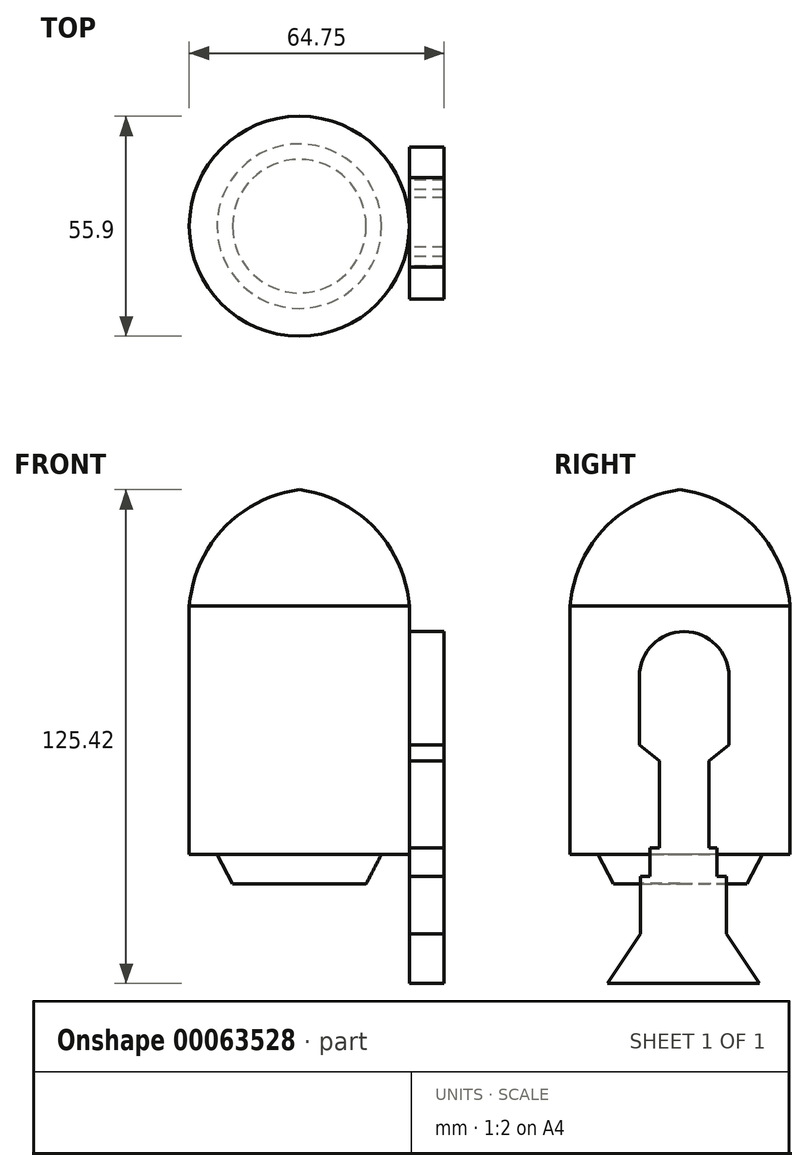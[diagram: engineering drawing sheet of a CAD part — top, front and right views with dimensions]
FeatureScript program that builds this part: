
annotation { "Feature Type Name" : "Feature", "Feature Type Description" : "" }
export const myFeature = defineFeature(function(context is Context, id is Id, definition is map)
    precondition{}
    {
        {
            var Q0;
            Q0=qCreatedBy(makeId("Front.planeOp"),FACE);
            var sketch = newSketch(context, id + "F0", { "sketchPlane" : qUnion([Q0])});
            skLineSegment(sketch, "E0", {"start": v(0, 29.6) * mm, "end": v(0, -70.4) * mm});
            skArc(sketch, "E1", {"start": v(27.95, 0) * mm, "mid": v(19.23, 19.76) * mm, "end": v(0, 29.6) * mm});
            skLineSegment(sketch, "E2", {"start": v(27.95, 0) * mm, "end": v(27.95, -63.03) * mm});
            skLineSegment(sketch, "E3", {"start": v(27.95, -63.03) * mm, "end": v(20.9, -63.03) * mm});
            skLineSegment(sketch, "E4", {"start": v(20.9, -63.03) * mm, "end": v(16.98, -70.53) * mm});
            skLineSegment(sketch, "E5", {"start": v(16.98, -70.53) * mm, "end": v(0, -70.4) * mm});
            skSolve(sketch);
        }
        {
            var Q0;
            Q0=makeQuery(id+"F0.imprint","IMPRINT",FACE,{"disambiguationData":[TD([[makeQuery(id+"F0.imprint","IMPRINT",EDGE,{"derivedFrom":sQuery(id+"F0.wireOp",EDGE,"E0")}),1.0]])]});
            var Q1;
            Q1=sQuery(id+"F0.wireOp",EDGE,"E0");
            revolve(context, id + "F1", {"entities" : qUnion([Q0]), "axis" : qUnion([Q1]), "revolveType" : RevolveType.FULL});
        }
        {
            var Q0;
            Q0=qCreatedBy(makeId("Right.planeOp"),FACE);
            cPlane(context, id + "F2", {"entities" : qUnion([Q0]), "cplaneType" : CPlaneType.OFFSET, "offset" : 28 * mm, "width" : 150 * mm, "height" : 150 * mm});
        }
        {
            var Q0;
            Q0=qCreatedBy(id+"F2.planeOp",FACE);
            var sketch = newSketch(context, id + "F3", { "sketchPlane" : qUnion([Q0])});
            skLineSegment(sketch, "E6", {"start": v(-10.35, -35.3) * mm, "end": v(-5.27, -39.28) * mm});
            skLineSegment(sketch, "E7", {"start": v(-5.27, -39.28) * mm, "end": v(-5.27, -61.37) * mm});
            skLineSegment(sketch, "E8", {"start": v(-5.27, -61.37) * mm, "end": v(-7.7, -61.37) * mm});
            skLineSegment(sketch, "E9", {"start": v(-7.7, -61.37) * mm, "end": v(-7.7, -68.65) * mm});
            skLineSegment(sketch, "E10", {"start": v(-7.7, -68.65) * mm, "end": v(-10.13, -68.65) * mm});
            skLineSegment(sketch, "E11", {"start": v(-10.13, -68.65) * mm, "end": v(-10.13, -83.23) * mm});
            skLineSegment(sketch, "E12", {"start": v(-10.13, -83.23) * mm, "end": v(-18.52, -95.82) * mm});
            skLineSegment(sketch, "E13", {"start": v(-18.52, -95.82) * mm, "end": v(20.13, -95.82) * mm});
            skLineSegment(sketch, "E14", {"start": v(20.13, -95.82) * mm, "end": v(11.74, -83.23) * mm});
            skLineSegment(sketch, "E15", {"start": v(11.74, -83.23) * mm, "end": v(11.74, -68.65) * mm});
            skLineSegment(sketch, "E16", {"start": v(11.74, -68.65) * mm, "end": v(9.31, -68.65) * mm});
            skLineSegment(sketch, "E17", {"start": v(9.31, -68.65) * mm, "end": v(9.31, -61.37) * mm});
            skLineSegment(sketch, "E18", {"start": v(9.31, -61.37) * mm, "end": v(7.32, -61.37) * mm});
            skLineSegment(sketch, "E19", {"start": v(7.32, -61.37) * mm, "end": v(7.32, -39.28) * mm});
            skLineSegment(sketch, "E20", {"start": v(7.32, -39.28) * mm, "end": v(12.4, -35.3) * mm});
            skLineSegment(sketch, "E21", {"start": v(12.4, -35.3) * mm, "end": v(12.4, -17.86) * mm});
            skLineSegment(sketch, "E22", {"start": v(-10.35, -35.3) * mm, "end": v(-10.35, -17.86) * mm});
            skArc(sketch, "E23", {"start": v(12.4, -17.86) * mm, "mid": v(1.03, -6.48) * mm, "end": v(-10.35, -17.86) * mm});
            skSolve(sketch);
        }
        {
            var Q0;
            Q0 = qSketchRegion(id + "F3", true);
            extrude(context, id + "F4", {"entities" : qUnion([Q0]), "depth" : 8.8 * mm});
        }
        {
            var Q0;
            Q0=makeQuery(id+"F4.opExtrude","SWEPT_EDGE",EDGE,{"disambiguationData":[OSD([sQuery(id+"F3.wireOp",EDGE,"E22"),sQuery(id+"F3.wireOp",EDGE,"E23")])]});
            cPlane(context, id + "F5", {"entities" : qUnion([Q0]), "cplaneType" : CPlaneType.LINE_ANGLE, "offset" : 150 * mm, "angle" : 30 * degree, "width" : 150 * mm, "height" : 150 * mm});
        }
        {
            var Q0;
            Q0=qCreatedBy(id+"F5.planeOp",FACE);
            cPlane(context, id + "F6", {"entities" : qUnion([Q0]), "cplaneType" : CPlaneType.OFFSET, "offset" : 40 * mm, "width" : 150 * mm, "height" : 150 * mm});
        }
    });
